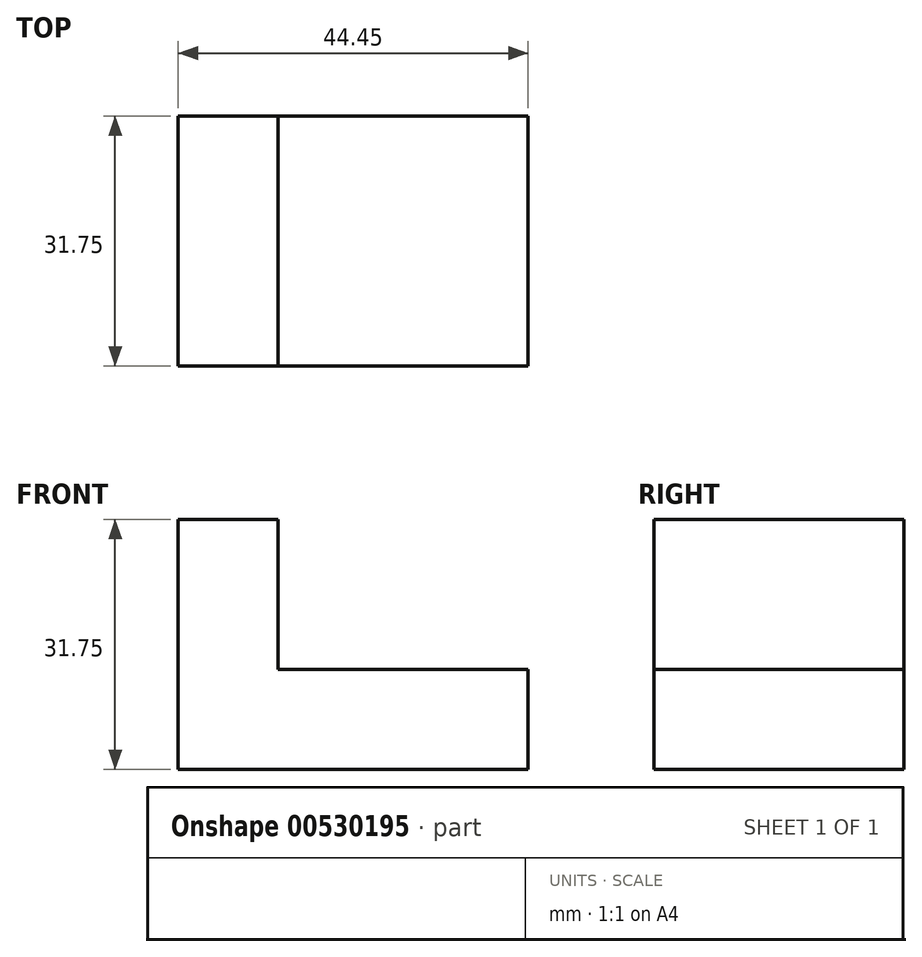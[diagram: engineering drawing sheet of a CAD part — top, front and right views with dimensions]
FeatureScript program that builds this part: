
annotation { "Feature Type Name" : "Feature", "Feature Type Description" : "" }
export const myFeature = defineFeature(function(context is Context, id is Id, definition is map)
    precondition{}
    {
        {
            var Q0;
            Q0=qCreatedBy(makeId("Front.planeOp"),FACE);
            var sketch = newSketch(context, id + "F0", { "sketchPlane" : qUnion([Q0])});
            skLineSegment(sketch, "E0", {"start": v(0, 31.75) * mm, "end": v(0, 0) * mm});
            skLineSegment(sketch, "E1", {"start": v(0, 0) * mm, "end": v(44.45, 0) * mm});
            skLineSegment(sketch, "E2", {"start": v(44.45, 0) * mm, "end": v(44.45, 12.7) * mm});
            skLineSegment(sketch, "E3", {"start": v(44.45, 12.7) * mm, "end": v(12.7, 12.7) * mm});
            skLineSegment(sketch, "E4", {"start": v(12.7, 12.7) * mm, "end": v(12.7, 31.75) * mm});
            skLineSegment(sketch, "E5", {"start": v(12.7, 31.75) * mm, "end": v(0, 31.75) * mm});
            skSolve(sketch);
        }
        {
            var Q0;
            Q0=makeQuery(id+"F0.imprint","IMPRINT",FACE,{"disambiguationData":[TD([[makeQuery(id+"F0.imprint","IMPRINT",EDGE,{"derivedFrom":sQuery(id+"F0.wireOp",EDGE,"E0")}),1.0]])]});
            extrude(context, id + "F1", {"entities" : qUnion([Q0]), "depth" : 31.75 * mm, "offsetDistance" : 25.4 * mm});
        }
    });
